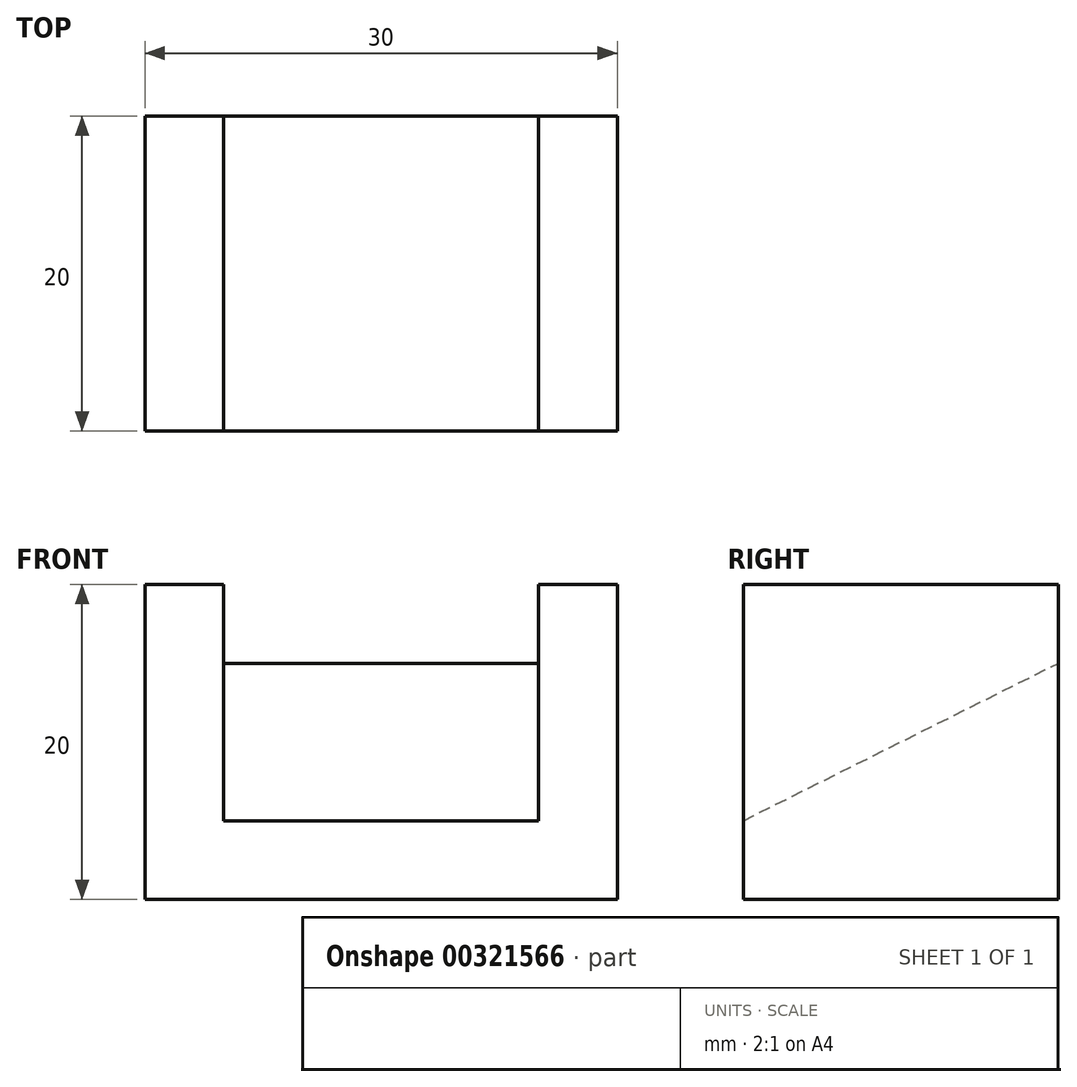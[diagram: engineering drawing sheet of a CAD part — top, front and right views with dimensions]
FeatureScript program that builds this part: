
annotation { "Feature Type Name" : "Feature", "Feature Type Description" : "" }
export const myFeature = defineFeature(function(context is Context, id is Id, definition is map)
    precondition{}
    {
        {
            var Q0;
            Q0=qCreatedBy(makeId("Top.planeOp"),FACE);
            var sketch = newSketch(context, id + "F0", { "sketchPlane" : qUnion([Q0])});
            skLineSegment(sketch, "E0.bottom", {"start": v(-15, 20) * mm, "end": v(15, 20) * mm});
            skLineSegment(sketch, "E0.top", {"start": v(-15, 0) * mm, "end": v(15, 0) * mm});
            skLineSegment(sketch, "E0.left", {"start": v(-15, 20) * mm, "end": v(-15, 0) * mm});
            skLineSegment(sketch, "E0.right", {"start": v(15, 20) * mm, "end": v(15, 0) * mm});
            skSolve(sketch);
        }
        {
            var Q0;
            Q0=makeQuery(id+"F0.imprint","IMPRINT",FACE,{"disambiguationData":[TD([[makeQuery(id+"F0.imprint","IMPRINT",EDGE,{"derivedFrom":sQuery(id+"F0.wireOp",EDGE,"E0.bottom")}),-1.0]])]});
            extrude(context, id + "F1", {"entities" : qUnion([Q0]), "depth" : 20 * mm});
        }
        {
            var Q0;
            Q0=qCreatedBy(makeId("Right.planeOp"),FACE);
            var sketch = newSketch(context, id + "F2", { "sketchPlane" : qUnion([Q0])});
            skLineSegment(sketch, "E1", {"start": v(0, 5) * mm, "end": v(20, 15) * mm});
            skLineSegment(sketch, "E2", {"start": v(20, 15) * mm, "end": v(20, 20) * mm});
            skLineSegment(sketch, "E3", {"start": v(20, 20) * mm, "end": v(0, 20) * mm});
            skLineSegment(sketch, "E4", {"start": v(0, 20) * mm, "end": v(0, 5) * mm});
            skSolve(sketch);
        }
        {
            var Q0;
            Q0 = qSketchRegion(id + "F2", true);
            extrude(context, id + "F3", {"entities" : qUnion([Q0]), "operationType" : NewBodyOperationType.REMOVE, "endBound" : BoundingType.SYMMETRIC, "oppositeDirection" : true, "depth" : 20 * mm});
        }
    });
